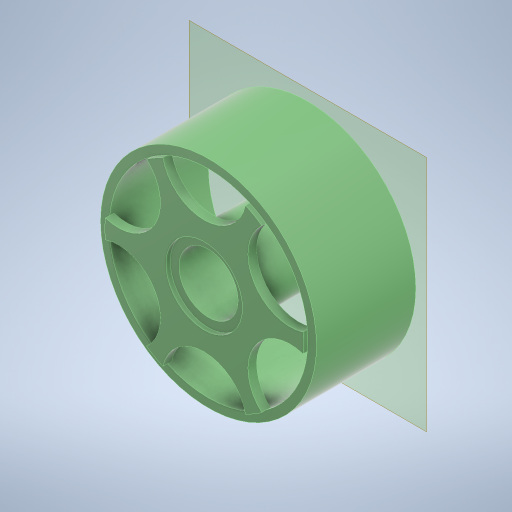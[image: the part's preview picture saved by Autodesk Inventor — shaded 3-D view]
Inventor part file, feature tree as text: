
AUTODESK INVENTOR PART (.ipt)
format: ipt  version: 2023 (Build 270158000, 158)  size: 320,512 bytes
history: native  units: in
note: dims shown in document units (in); Inventor stores cm internally (conversion verified against a paired STEP export)
features: extrude x3, sketch x3, plane x1
ambient origin geometry x8: Origin, YZ Plane, XZ Plane, XY Plane, X Axis, Y Axis, Z Axis, Center Point
bodies: Solid1 (feature_tree)
feature tree (7):
  extrude  "Extrusion1"  Depth=0.05in
  plane  "Work Plane1"
  extrude  "Extrusion2"  Depth=0.05in
  extrude  "Extrusion4"  TaperAngle=0.0deg  [1 undecoded]
  sketch  "Sketch1"  dims[d0=0.44in d1=0.05in]
  sketch  "Sketch2"  dims[d2=0.35in d3=0.05in]
  sketch  "Sketch3"  dims[d4=0.57in d5=0.0in d6=0.0in d7=0.05in d8=0.0in d9=2.3622in d11=360.0deg d15=0.05in d16=0.0in d10=0.0344in]
note: 1 required parameter value undecoded (feature->parameter linkage not recoverable at this tier; creation-order binding heuristic only, values carry confidence <= 0.55)
